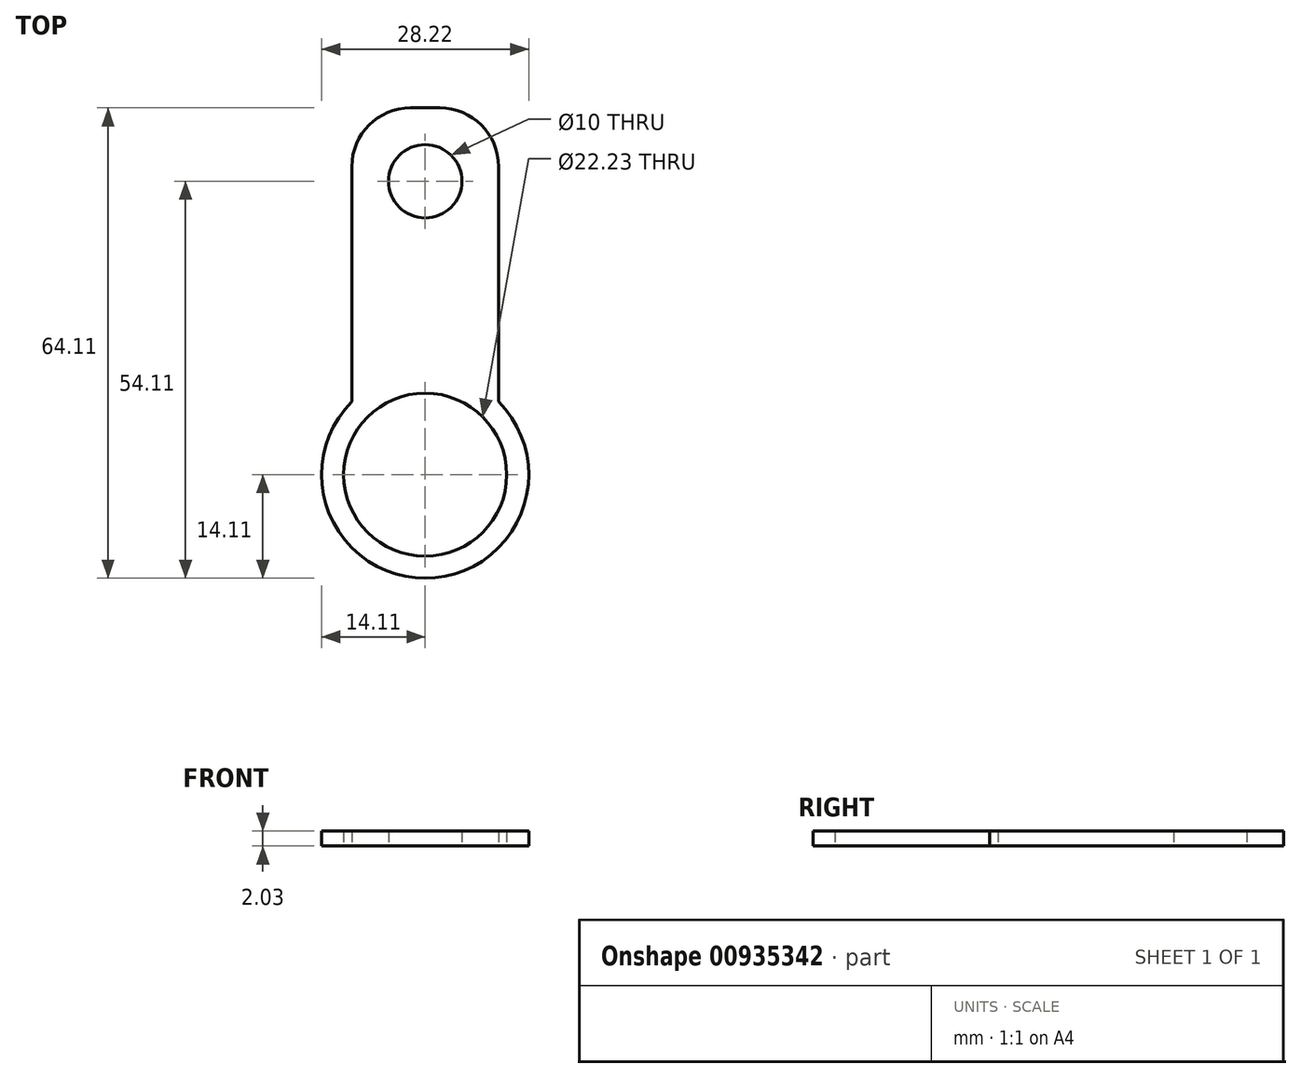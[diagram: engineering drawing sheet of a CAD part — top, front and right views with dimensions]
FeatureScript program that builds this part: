
annotation { "Feature Type Name" : "Feature", "Feature Type Description" : "" }
export const myFeature = defineFeature(function(context is Context, id is Id, definition is map)
    precondition{}
    {
        {
            var Q0;
            Q0=qCreatedBy(makeId("Top.planeOp"),FACE);
            var sketch = newSketch(context, id + "F0", { "sketchPlane" : qUnion([Q0])});
            skLineSegment(sketch, "E0.top", {"start": v(-2, 50) * mm, "end": v(2, 50) * mm});
            skLineSegment(sketch, "E0.left", {"start": v(-10, 9.96) * mm, "end": v(-10, 42) * mm});
            skLineSegment(sketch, "E0.right", {"start": v(10, 9.96) * mm, "end": v(10, 42) * mm});
            skCircle(sketch, "E1", {"center": v(0, 40) * mm, "radius": 5 * mm});
            skLineSegment(sketch, "E2", {"start": v(5, 40) * mm, "end": v(10, 40) * mm, "construction": true});
            skLineSegment(sketch, "E3", {"start": v(0, 45) * mm, "end": v(0, 50) * mm, "construction": true});
            skPoint(sketch, "E4.visualSharp", {"position": v(-10, 50) * mm});
            skArc(sketch, "E4.filletArc", {"start": v(-2, 50) * mm, "mid": v(-7.66, 47.66) * mm, "end": v(-10, 42) * mm});
            skPoint(sketch, "E5.visualSharp", {"position": v(10, 50) * mm});
            skArc(sketch, "E5.filletArc", {"start": v(10, 42) * mm, "mid": v(7.66, 47.66) * mm, "end": v(2, 50) * mm});
            skCircle(sketch, "E6", {"center": v(0, 0) * mm, "radius": 11.11 * mm});
            skArc(sketch, "E7", {"start": v(-10, 9.96) * mm, "mid": v(0, -14.11) * mm, "end": v(10, 9.96) * mm});
            skLineSegment(sketch, "E8", {"start": v(11.11, 0) * mm, "end": v(14.11, 0) * mm, "construction": true});
            skSolve(sketch);
        }
        {
            var Q0;
            Q0=qSketchRegion(id+"F0",true);
            extrude(context, id + "F1", {"entities" : qUnion([Q0]), "depth" : 2.03 * mm, "offsetDistance" : 25 * mm});
        }
    });
